# Revit family: Singola One Piece Free Standing Bath - White
name_source: partatom
category: Plumbing Fixtures
units: mm (PartAtom-declared; Revit-internal decimal feet)

## family parameters
Always vertical = Yes
Cut with Voids When Loaded = No
Enable Cutting in Views = No
Maintain Annotation Orientation = No
OmniClass Number = 23.45.00.00
OmniClass Title = Sanitary, Laundry, and Cleaning Equipment
Part Type = Normal
Room Calculation Point = No
Round Connector Dimension = Use Diameter
Shared = No
Work Plane-Based = No

## types (1)
- Singola One Piece Free Standing Bath - White
    Category = Baths
    Colour = White
    Default Elevation = 0 mm  [stored 0 ft]
    Depth = 785 mm
    Height = 550 mm  [stored 1.80446 ft]
    Manufacturer = Lecico SA
    Material = Sanitary Grade Acrylic
    Model = Singola One Piece Free Standing Bath - White
    Porcelain = Porcelain White
    Product Code = BATSINGOLA000BS
    Stainless Steel = <By Category>
    Technical Dimensions = W1690 x H550 x D785mm
    URL = https://www.lecicosa.co.za
    Width = 1690 mm

note: [stored X ft] marks values corroborated as IEEE doubles in the binary element streams (Revit-internal decimal feet)

## geometry (parser evidence)
native form markers: Blend x2, Sweep x2
no freeform markers — native parametric forms only
